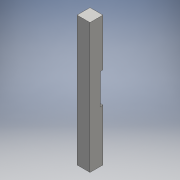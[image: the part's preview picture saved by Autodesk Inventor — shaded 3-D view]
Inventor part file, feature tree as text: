
AUTODESK INVENTOR PART (.ipt)
format: ipt  version: 2016 SP1 (Build 200210100, 210)  size: 102,400 bytes
history: native  units: mm
features: extrude x2, sketch x2
ambient origin geometry x8: Origin, YZ Plane, XZ Plane, XY Plane, X Axis, Y Axis, Z Axis, Center Point
bodies: Solid1 (feature_tree)
feature tree (4):
  extrude  "Extrusion1"  Depth=20.0mm
  extrude  "Extrusion2"  Depth=4.0mm
  sketch  "Sketch1"  dims[d0=20.0mm d1=20.0mm]
  sketch  "Sketch2"  dims[d2=10.0mm d3=10.0mm d4=200.0mm d5=0.0mm d6=47.0mm d7=80.0mm d8=4.0mm d9=0.0mm]
